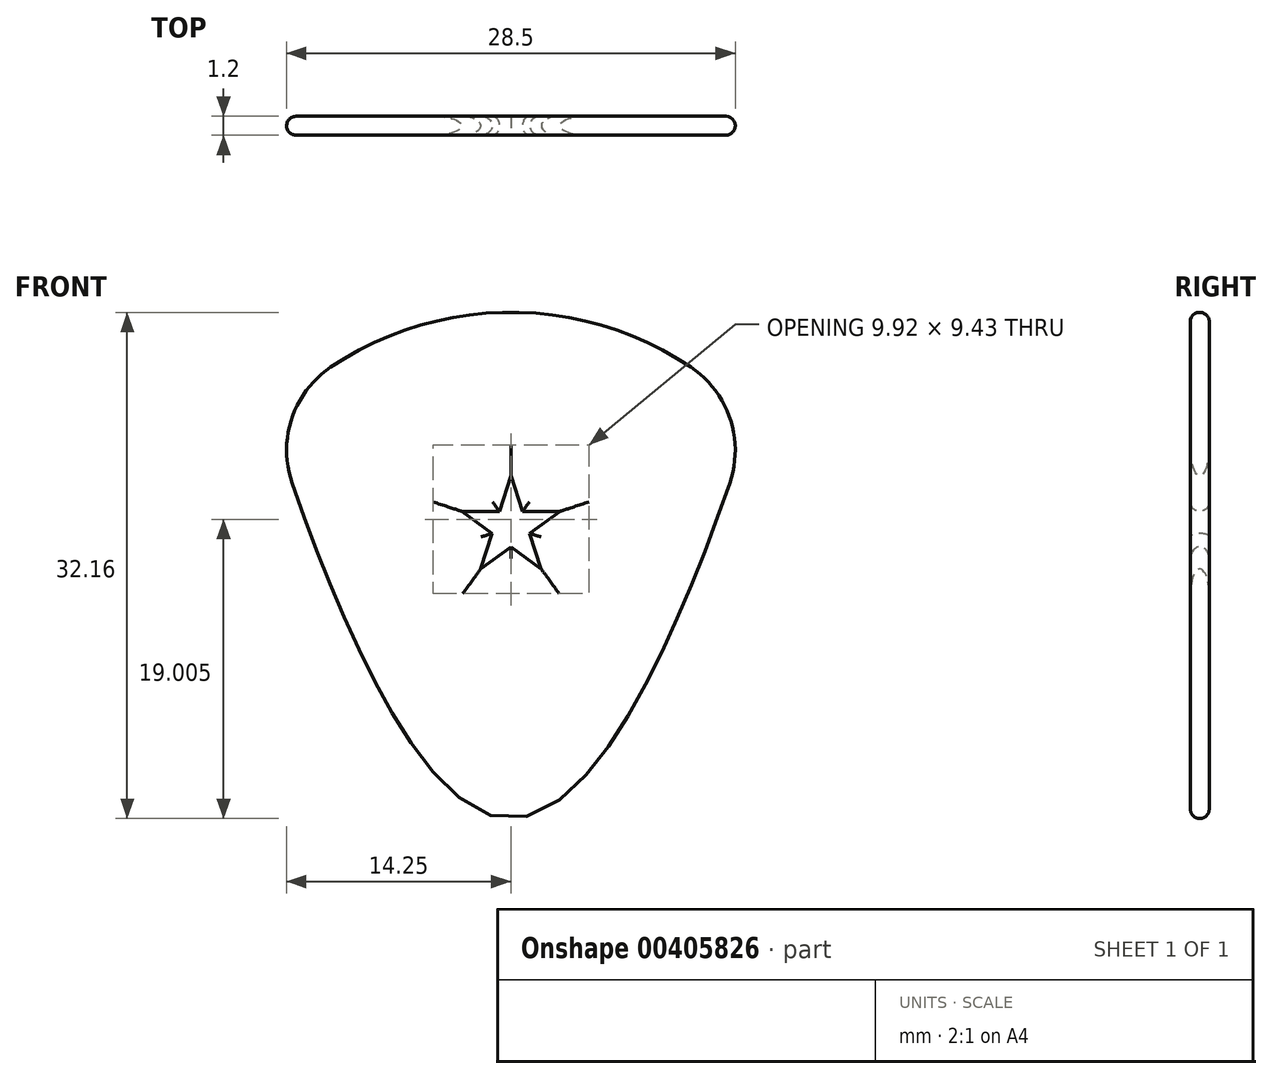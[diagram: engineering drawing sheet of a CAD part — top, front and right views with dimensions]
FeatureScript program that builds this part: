
annotation { "Feature Type Name" : "Feature", "Feature Type Description" : "" }
export const myFeature = defineFeature(function(context is Context, id is Id, definition is map)
    precondition{}
    {
        {
            var Q0;
            Q0=qCreatedBy(makeId("Front.planeOp"),FACE);
            var sketch = newSketch(context, id + "F0", { "sketchPlane" : qUnion([Q0])});
            skLineSegment(sketch, "E0", {"start": v(0, 25.37) * mm, "end": v(15.24, 25.37) * mm, "construction": true});
            skLineSegment(sketch, "E1", {"start": v(0, 25.37) * mm, "end": v(-15.24, 25.37) * mm, "construction": true});
            skFitSpline(sketch, "E2", {"points": [v(-15.24, 25.37) * mm, v(0, 0) * mm, v(15.24, 25.37) * mm], "startDerivative": vector(26.17, -82.3) * mm, "endDerivative": vector(26.17, 82.3) * mm});
            skArc(sketch, "E3", {"start": v(11.44, 28.67) * mm, "mid": v(0, 32.16) * mm, "end": v(-11.44, 28.67) * mm});
            skArc(sketch, "E4.filletArc", {"start": v(-11.44, 28.67) * mm, "mid": v(-13.92, 25.42) * mm, "end": v(-13.9, 21.33) * mm});
            skArc(sketch, "E5.filletArc", {"start": v(13.9, 21.33) * mm, "mid": v(13.92, 25.42) * mm, "end": v(11.44, 28.67) * mm});
            skLineSegment(sketch, "E6", {"start": v(10.88, 11.66) * mm, "end": v(-10.88, 11.66) * mm, "construction": true});
            skPoint(sketch, "E7.MirrorCS.start.orphan", {"position": v(11.44, 28.67) * mm});
            skPoint(sketch, "E8.MirrorCS.start.orphan", {"position": v(13.9, 21.33) * mm});
            skCircle(sketch, "E9.cCircle", {"center": v(0, 18.5) * mm, "radius": 1.25 * mm, "construction": true});
            skLineSegment(sketch, "E9.0", {"start": v(0.73, 19.52) * mm, "end": v(1.19, 18.12) * mm});
            skLineSegment(sketch, "E9.1", {"start": v(1.19, 18.12) * mm, "end": v(0, 17.26) * mm});
            skLineSegment(sketch, "E9.2", {"start": v(0, 17.26) * mm, "end": v(-1.19, 18.12) * mm});
            skLineSegment(sketch, "E9.3", {"start": v(-1.19, 18.12) * mm, "end": v(-0.73, 19.52) * mm});
            skLineSegment(sketch, "E9.4", {"start": v(-0.73, 19.52) * mm, "end": v(0.73, 19.52) * mm});
            skLineSegment(sketch, "E10", {"start": v(-0.73, 19.52) * mm, "end": v(0, 21.78) * mm});
            skLineSegment(sketch, "E11", {"start": v(0, 21.78) * mm, "end": v(0.73, 19.52) * mm});
            skLineSegment(sketch, "E12", {"start": v(-0.73, 19.52) * mm, "end": v(-3.11, 19.52) * mm});
            skLineSegment(sketch, "E13", {"start": v(-3.11, 19.52) * mm, "end": v(-1.19, 18.12) * mm});
            skLineSegment(sketch, "E14", {"start": v(0.73, 19.52) * mm, "end": v(3.11, 19.52) * mm});
            skLineSegment(sketch, "E15", {"start": v(3.11, 19.52) * mm, "end": v(1.19, 18.12) * mm});
            skLineSegment(sketch, "E16", {"start": v(-1.19, 18.12) * mm, "end": v(-1.92, 15.86) * mm});
            skLineSegment(sketch, "E17", {"start": v(-1.92, 15.86) * mm, "end": v(0, 17.26) * mm});
            skLineSegment(sketch, "E18", {"start": v(0, 17.26) * mm, "end": v(1.92, 15.86) * mm});
            skLineSegment(sketch, "E19", {"start": v(1.92, 15.86) * mm, "end": v(1.19, 18.12) * mm});
            skSolve(sketch);
        }
        {
            var Q0;
            Q0=makeQuery(id+"F0.imprint","IMPRINT",FACE,{"disambiguationData":[TD([[makeQuery(id+"F0.imprint","IMPRINT",EDGE,{"derivedFrom":sQuery(id+"F0.wireOp",EDGE,"E2")}),1.0]])]});
            var Q1;
            Q1=makeQuery(id+"F0.imprint","IMPRINT",FACE,{"disambiguationData":[TD([[makeQuery(id+"F0.imprint","IMPRINT",EDGE,{"derivedFrom":sQuery(id+"F0.wireOp",EDGE,"E4.filletArc")}),-1.0]])]});
            var Q2;
            Q2=makeQuery(id+"F0.imprint","IMPRINT",FACE,{"disambiguationData":[TD([[makeQuery(id+"F0.imprint","IMPRINT",EDGE,{"derivedFrom":sQuery(id+"F0.wireOp",EDGE,"E5.filletArc")}),-1.0]])]});
            extrude(context, id + "F1", {"entities" : qUnion([Q0, Q1, Q2]), "depth" : 1.2 * mm, "offsetDistance" : 25 * mm});
        }
        {
            var Q0;
            Q0=makeQuery(id+"F1.opExtrude","CAP_EDGE",EDGE,{"disambiguationData":[OSD([sQuery(id+"F0.wireOp",EDGE,"E2")])],"isStart":true});
            var Q1;
            Q1=makeQuery(id+"F1.opExtrude","CAP_EDGE",EDGE,{"disambiguationData":[OSD([sQuery(id+"F0.wireOp",EDGE,"7ea5a1a3-41db-4b7b-b8c7-d5a5067a70c7")])],"isStart":true});
            var Q2;
            Q2=makeQuery(id+"F1.opExtrude","CAP_EDGE",EDGE,{"disambiguationData":[OSD([sQuery(id+"F0.wireOp",EDGE,"7ea5a1a3-41db-4b7b-b8c7-d5a5067a70c7")])],"isStart":false});
            var Q3;
            Q3=makeQuery(id+"F1.opExtrude","CAP_EDGE",EDGE,{"disambiguationData":[OSD([sQuery(id+"F0.wireOp",EDGE,"E2")])],"isStart":false});
            var Q4;
            Q4=makeQuery(id+"F1.opExtrude","CAP_EDGE",EDGE,{"disambiguationData":[OSD([sQuery(id+"F0.wireOp",EDGE,"E3")])],"isStart":false});
            var Q5;
            Q5=makeQuery(id+"F1.opExtrude","CAP_EDGE",EDGE,{"disambiguationData":[OSD([sQuery(id+"F0.wireOp",EDGE,"e8d5be13-d336-4b08-b9e4-ac300f1e6e79")])],"isStart":false});
            var Q6;
            Q6=makeQuery(id+"F1.opExtrude","CAP_EDGE",EDGE,{"disambiguationData":[OSD([sQuery(id+"F0.wireOp",EDGE,"E8.MirrorCS")])],"isStart":false});
            var Q7;
            Q7=makeQuery(id+"F1.opExtrude","CAP_EDGE",EDGE,{"disambiguationData":[OSD([sQuery(id+"F0.wireOp",EDGE,"e8d5be13-d336-4b08-b9e4-ac300f1e6e79")])],"isStart":true});
            var Q8;
            Q8=makeQuery(id+"F1.opExtrude","CAP_EDGE",EDGE,{"disambiguationData":[OSD([sQuery(id+"F0.wireOp",EDGE,"E3")])],"isStart":true});
            var Q9;
            Q9=makeQuery(id+"F1.opExtrude","CAP_EDGE",EDGE,{"disambiguationData":[OSD([sQuery(id+"F0.wireOp",EDGE,"E7.MirrorCS")])],"isStart":true});
            var Q10;
            Q10=makeQuery(id+"F1.opExtrude","CAP_EDGE",EDGE,{"disambiguationData":[OSD([sQuery(id+"F0.wireOp",EDGE,"E8.MirrorCS")])],"isStart":true});
            var Q11;
            Q11=makeQuery(id+"F1.opExtrude","CAP_EDGE",EDGE,{"disambiguationData":[OSD([sQuery(id+"F0.wireOp",EDGE,"E10")])],"isStart":false});
            var Q12;
            Q12=makeQuery(id+"F1.opExtrude","CAP_EDGE",EDGE,{"disambiguationData":[OSD([sQuery(id+"F0.wireOp",EDGE,"E11")])],"isStart":false});
            var Q13;
            Q13=makeQuery(id+"F1.opExtrude","CAP_EDGE",EDGE,{"disambiguationData":[OSD([sQuery(id+"F0.wireOp",EDGE,"E14")])],"isStart":false});
            var Q14;
            Q14=makeQuery(id+"F1.opExtrude","CAP_EDGE",EDGE,{"disambiguationData":[OSD([sQuery(id+"F0.wireOp",EDGE,"E15")])],"isStart":false});
            var Q15;
            Q15=makeQuery(id+"F1.opExtrude","CAP_EDGE",EDGE,{"disambiguationData":[OSD([sQuery(id+"F0.wireOp",EDGE,"E19")])],"isStart":false});
            var Q16;
            Q16=makeQuery(id+"F1.opExtrude","CAP_EDGE",EDGE,{"disambiguationData":[OSD([sQuery(id+"F0.wireOp",EDGE,"E18")])],"isStart":false});
            var Q17;
            Q17=makeQuery(id+"F1.opExtrude","CAP_EDGE",EDGE,{"disambiguationData":[OSD([sQuery(id+"F0.wireOp",EDGE,"E17")])],"isStart":false});
            var Q18;
            Q18=makeQuery(id+"F1.opExtrude","CAP_EDGE",EDGE,{"disambiguationData":[OSD([sQuery(id+"F0.wireOp",EDGE,"E16")])],"isStart":false});
            var Q19;
            Q19=makeQuery(id+"F1.opExtrude","CAP_EDGE",EDGE,{"disambiguationData":[OSD([sQuery(id+"F0.wireOp",EDGE,"E13")])],"isStart":false});
            var Q20;
            Q20=makeQuery(id+"F1.opExtrude","CAP_EDGE",EDGE,{"disambiguationData":[OSD([sQuery(id+"F0.wireOp",EDGE,"E12")])],"isStart":false});
            var Q21;
            Q21=makeQuery(id+"F1.opExtrude","CAP_EDGE",EDGE,{"disambiguationData":[OSD([sQuery(id+"F0.wireOp",EDGE,"E10")])],"isStart":true});
            var Q22;
            Q22=makeQuery(id+"F1.opExtrude","CAP_EDGE",EDGE,{"disambiguationData":[OSD([sQuery(id+"F0.wireOp",EDGE,"E11")])],"isStart":true});
            var Q23;
            Q23=makeQuery(id+"F1.opExtrude","CAP_EDGE",EDGE,{"disambiguationData":[OSD([sQuery(id+"F0.wireOp",EDGE,"E14")])],"isStart":true});
            var Q24;
            Q24=makeQuery(id+"F1.opExtrude","CAP_EDGE",EDGE,{"disambiguationData":[OSD([sQuery(id+"F0.wireOp",EDGE,"E15")])],"isStart":true});
            var Q25;
            Q25=makeQuery(id+"F1.opExtrude","CAP_EDGE",EDGE,{"disambiguationData":[OSD([sQuery(id+"F0.wireOp",EDGE,"E18")])],"isStart":true});
            var Q26;
            Q26=makeQuery(id+"F1.opExtrude","CAP_EDGE",EDGE,{"disambiguationData":[OSD([sQuery(id+"F0.wireOp",EDGE,"E19")])],"isStart":true});
            var Q27;
            Q27=makeQuery(id+"F1.opExtrude","CAP_EDGE",EDGE,{"disambiguationData":[OSD([sQuery(id+"F0.wireOp",EDGE,"E17")])],"isStart":true});
            var Q28;
            Q28=makeQuery(id+"F1.opExtrude","CAP_EDGE",EDGE,{"disambiguationData":[OSD([sQuery(id+"F0.wireOp",EDGE,"E16")])],"isStart":true});
            var Q29;
            Q29=makeQuery(id+"F1.opExtrude","CAP_EDGE",EDGE,{"disambiguationData":[OSD([sQuery(id+"F0.wireOp",EDGE,"E13")])],"isStart":true});
            var Q30;
            Q30=makeQuery(id+"F1.opExtrude","CAP_EDGE",EDGE,{"disambiguationData":[OSD([sQuery(id+"F0.wireOp",EDGE,"E12")])],"isStart":true});
            fillet(context, id + "F2", {"entities" : qUnion([Q0, Q1, Q2, Q3, Q4, Q5, Q6, Q7, Q8, Q9, Q10, Q11, Q12, Q13, Q14, Q15, Q16, Q17, Q18, Q19, Q20, Q21, Q22, Q23, Q24, Q25, Q26, Q27, Q28, Q29, Q30]), "tangentPropagation" : true, "radius" : .6 * mm, "defaultsChanged" : false, "vertexSettings" : [], "allowEdgeOverflow" : false});
        }
    });
